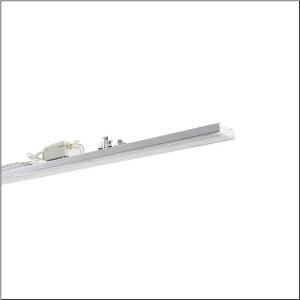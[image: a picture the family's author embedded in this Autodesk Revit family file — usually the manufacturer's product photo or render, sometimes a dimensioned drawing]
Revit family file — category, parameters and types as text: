
# Revit family: licross_r__21_recessed_mo_52tl12dn455g_fe02
name_source: partatom
category: Lighting Fixtures
units: mm (PartAtom-declared; Revit-internal decimal feet)

## family parameters
Cut with Voids When Loaded = No
Host = Face
Light Source = No
Part Type = Normal
Room Calculation Point = No
Round Connector Dimension = Use Diameter
Shared = No

## types (1)
- --- (1 x LED, 5500 lm, 29.6 W, 4000K)
    Apparent Load = 30 VA
    CIE Flux Codes = 72 92 99 100 100
    Color Rendering = 80
    Color Temperature = 4000K
    Default Elevation = 1800 mm
    Description = Licross® 21 Recessed MO, luminaire insert, of sheet steel, galvanised, coil coated, white, length: 1.500mm, width: 66mm, height: 67mm, LED rated luminous flux: 5.500lm, light colour: 840, control gear: DALI 2, with plug, 5-pole, with phase selection, mains connection: 220..240V, AC, 50/60Hz, rated input power: 30W, halogen-free wiring, primary optical cover: cover, of PMMA, light emission: direct distribution, primary light characteristic: symmetric, protection rating (complete): IP40, insulation class (complete): insulation class I (protective earthing), certification: CE, ENEC, VDE, UKCA, protection symbol: D if used in an environment without relevant dust loads with corresponding accessories, impact resistance: IK06, permissible ambient temperature for indoor applications: -25..+45°C, corresponds to IFS (International Featured Standards) requirements for safety and quality in the food industry, reducing of maximum allowable ambient temperature of 5°C with ceiling mounting, LABS conformity tested according to VDMA 24364:2018-05, packaging unit: 1 piece
    Height = 58 mm
    Lamp = 1 x LED
    Lamp Light Flux = 5500 lm
    Lamp Power = 29.6 W
    Lamp count = 1
    Length = 1500 mm
    Luminous efficacy = 186 lm/W
    Manufacturer = Siteco
    ModVariant = No
    Model = 52TL12DN455G
    Mounting Place = Ceiling
    Mounting Type = Pendant
    Number of Poles = 1
    OnlyDefault = Yes
    Power Factor = 1
    Product Name = Licross® 21 Recessed MO
    Product group = luminaire insert
    ProductGroupID = 901
    Protection Class = Protection class I
    Protection Degree = IP 40
    RLX_Detail_Level = 1
    RLX_Emergency_Light_Flux = 0 lm
    RLX_Emergency_Type = 0
    RLX_Emergency_Type_DB = No
    RlxData = <blob elided: 23933 chars, md5=258cc717>
    Socket = socket
    Standby Power = 0 W
    System Light Flux = 5500 lm
    System Power = 30 W
    Type Comments = factory setting: luminous flux: 100 % | dim-lin: 254 | 200 mA
    Type Image = l_1296930.jpg
    URL = http://relux.com
    VarID = @adj_057789
    Voltage = 0 V
    Weight = 0.00 kg
    Width = 66 mm

## geometry (parser evidence)
native form markers: Blend x4, Sweep x12
no freeform markers — native parametric forms only
